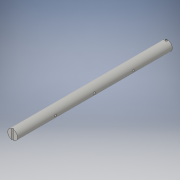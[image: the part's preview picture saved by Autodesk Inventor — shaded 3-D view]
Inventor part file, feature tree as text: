
AUTODESK INVENTOR PART (.ipt)
format: ipt  version: 2016 (Build 200138000, 138)  size: 134,144 bytes
history: native  units: in
note: dims shown in document units (in); Inventor stores cm internally (conversion verified against a paired STEP export)
features: extrude x4, sketch x3
ambient origin geometry x8: Origin, YZ Plane, XZ Plane, XY Plane, X Axis, Y Axis, Z Axis, Center Point
bodies: Solid1 (feature_tree)
feature tree (7):
  extrude  "Extrusion1"  Depth=8.0in TaperAngle=0.0deg
  extrude  "Extrusion4"  Depth=0.06in
  extrude  "Extrusion8"  Depth=2.0in TaperAngle=0.0deg
  extrude  "Extrusion9"  Depth=2.0in
  sketch  "Sketch1"  dims[d0=0.5in d1=8.0in d2=0.0in]
  sketch  "Sketch4"  dims[d13=0.06in d15=0.06in]
  sketch  "Sketch7"  dims[d16=0.1in d17=0.6in d18=0.0in d19=0.1in d20=0.06in d21=0.05in d26=0.5in d27=0.06in d42=2.0in d43=0.1in d44=2.0in d45=0.1in d46=2.0in d47=0.1in d48=1.0in d49=0.0in d50=1.0in d51=0.0in]
